# Revit family: IS_ConceptEasyBox_Multiproduct_BIM_GB_A5880;A5878;A5879
name_source: partatom
category: Plumbing Fixtures
revit_build: Autodesk Revit MEP 2016 (Build: 20161004_0715(x64)
units: mm (PartAtom-declared; Revit-internal decimal feet)

## family parameters
Cut with Voids When Loaded = Yes
Host = Face
OmniClass Number = 23.45.05.14.17
OmniClass Title = Showers
Part Type = Normal
Room Calculation Point = No
Round Connector Dimension = Use Diameter
Shared = Yes

## types (4) — shared parameters
AreaUnits = millimeters
Assembly Code = C1030200
AssetType = Fixed
Brand = Ideal Standard
ConnectionType = Plumbing
Default Elevation = 1100 mm
DurationUnit = year
ExpectedLife = 30
FaucetFunction = MIXED
FaucetOperation = Other
FaucetTopDescription = Handwheels
FaucetType = Other
Finish = Chrome
IfcExportAs = IfcValveType
IfcExportType = FAUCET
InstallationDate = 1900-12-31T23:59:59
InstallationInstructions = www.idealspec.co.uk/resources.html
LinearUnits = millimeters
ManufacturerURL = www.idealspec.co.uk
NBSDescription = Shower mixers
NBSReference = 45-35-70/335
NettWeight = 3 Kg
NominalHeight = 164 mm  [stored 0.538058 ft]
NominalLength = 185 mm  [stored 0.606955 ft]
NominalWidth = 185 mm  [stored 0.606955 ft]
Shape = Sculptured
Size = 164 x 185 x 185 mm
Space = Internal
SpareParts = www.fastpart-spares.co.uk
SustainabilityPerformance = Can be recycled
TestPressure = 10 Bar
URL = www.idealspec.co.uk
Uniclass2 = Pr_40_20_87_81
ValveMatl = ISI_IdealStandard_Brassware_Chrome3_Render
Version = 1
VolumeUnits = Litres
WarrantyDescription = Manufacturers warranty
WarrantyDurationParts = 5
WarrantyDurationUnit = year
WarrantyStartDate = 1900-12-31T23:59:59

## per-type parameters (varying)
| type | A5877AA/A5879AA | A5878AA/A5880AA | BIMObjectName | BarCode | Description | Features | Model | ModelNumber | ModelReference | Name | ProductInformation |
| A5879AA - Concept Easybox Slim Built-in Thermostatic Bath Shower Mixer Round Faceplate | Yes | No | ISI_IdealStandard_ShowerMixers_ConceptEasyBox_A5879 | 4015413330213 | Concept easybox slim built-in thermostatic bath shower mixer round faceplate | Slim built-in thermostatic bath shower mixer round faceplate | A5879AA | A5879AA | Concept easybox slim built-in thermostatic bath shower mixer round faceplate | ShowerMixers_ConceptEasyBox_A5879_IdealStandard | www.idealspec.co.uk/assets/datasheet/A5879AA |
| A5878AA - Concept Easybox Slim Built-in Thermostatic Bath Shower Mixer Square Faceplate | No | Yes | ISI_IdealStandard_ShowerMixers_ConceptEasyBox_A5878 |  | Concept easybox slim built-in thermostatic bath shower mixer square faceplate | Slim built-in thermostatic bath shower mixer square faceplate | A5878AA | A5878AA | Concept easybox slim built-in thermostatic bath shower mixer square faceplate | ShowerMixers_ConceptEasyBox_A5878_IdealStandard | www.idealspec.co.uk/assets/datasheet/A5878AA |
| A5880AA - Concept Easybox Slim Built-in Bath Shower Mixer Square Faceplate | No | Yes | ISI_IdealStandard_ShowerMixers_ConceptEasyBox_A5880 |  | Concept Easybox Slim Built-in Bath Shower Mixer Square Faceplate | Slim built-in thermostatic bath shower mixer with square faceplate. Consists of brass mixer, plastic installation box, mounting bracket, faceplate and handles. | A5880AA | A5880AA | Concept Easybox Slim Built-in Bath Shower Mixer Square Faceplate | ShowerMixers_ConceptEasyBox_A5880_IdealStandard | www.idealspec.co.uk/assets/datasheet/A5880AA |
| A5877AA - Concept Easybox Slim Built-in Shower Mixer Round Faceplate | Yes | No | ISI_IdealStandard_ShowerMixers_ConceptEasyBox_A5877 |  | Concept Easybox Slim Built-in Shower Mixer Round Faceplate | Slim built-in thermostatic bath shower mixer round faceplate | A5877AA | A5877AA | Concept Easybox Slim Built-in Shower Mixer Round Faceplate | ShowerMixers_ConceptEasyBox_A5877_IdealStandard | www.idealspec.co.uk/assets/datasheet/A5877AA |

note: [stored X ft] marks values corroborated as IEEE doubles in the binary element streams (Revit-internal decimal feet)

## geometry (parser evidence)
native form markers: Sweep x5
no freeform markers — native parametric forms only
